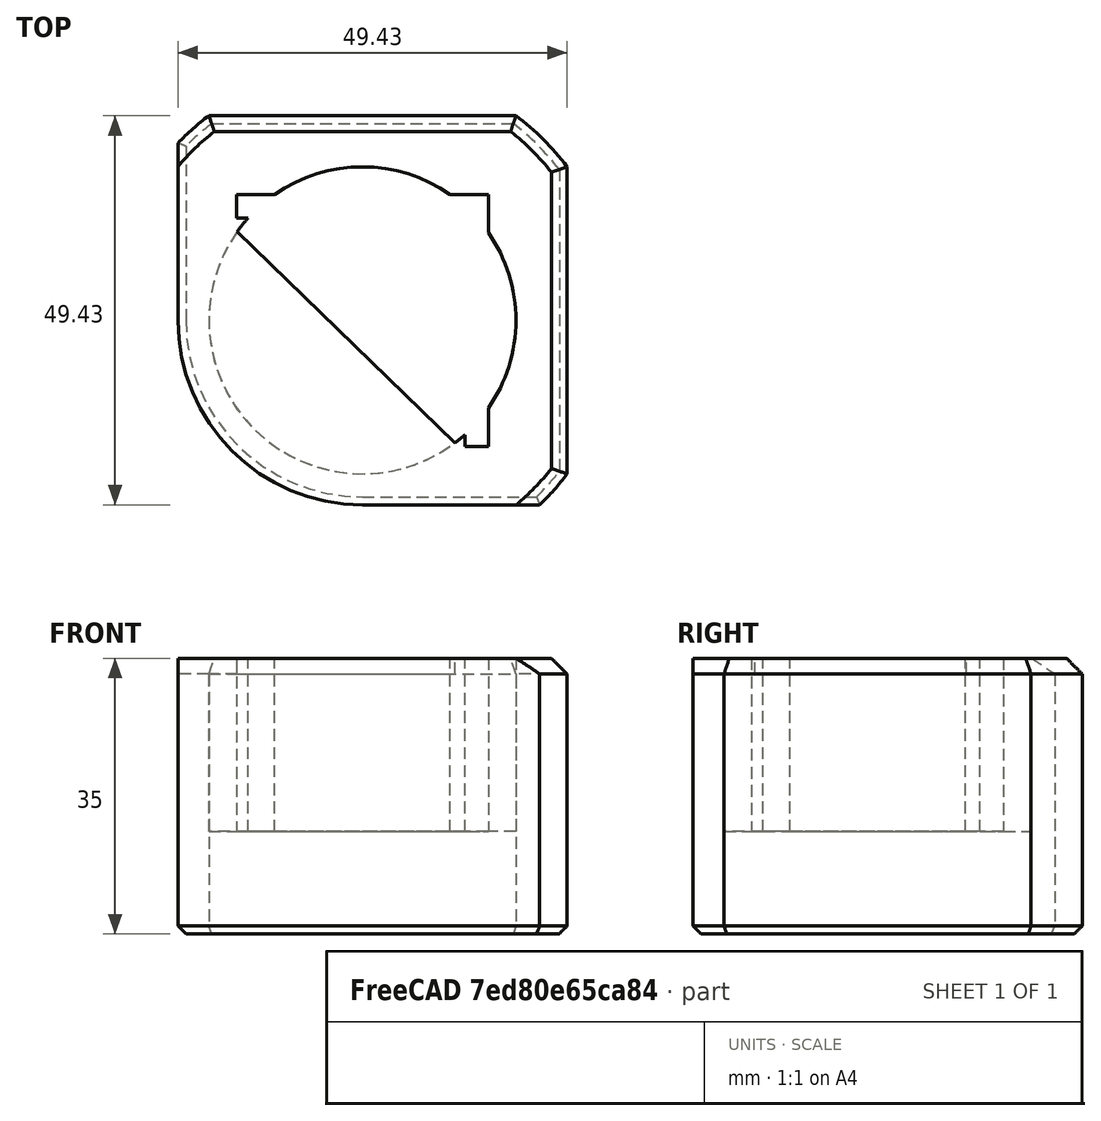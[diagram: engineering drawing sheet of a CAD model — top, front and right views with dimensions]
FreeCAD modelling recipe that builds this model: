
FCSTD DOCUMENT  (FreeCAD 0.19R)
Label: tankfeettallRC1
License: All rights reserved
LicenseURL: http://en.wikipedia.org/wiki/All_rights_reserved
objects: Sketcher::SketchObject×6, PartDesign::Pocket×4, PartDesign::Pad×2, PartDesign::Chamfer×2, PartDesign::Body×1, Mesh::Feature×1
note: 23 computed .brp shape members not serialized (recipe doc carries the construction recipe); baked Part::Feature solids carry a one-line shape summary decoded from their .brp

FEATURE [Sketcher::SketchObject] Sketch
  FullyConstrained = true
  MapMode = 5
  Support = -> [XY_Plane]
  sketch-geometry (1):
    g0: Circle CenterX=0 CenterY=0 CenterZ=0 NormalX=0 NormalY=0 NormalZ=1 AngleXU=0 Radius=32.5
  constraints (2):
    c: Coincident(g0,g-1)
    c: Diameter(g0) = 65
FEATURE [PartDesign::Pad] Pad
  Direction = (1,1,1)
  Length = 35
  Length2 = 100
  Profile = -> Sketch
  Type = 0
FEATURE [Sketcher::SketchObject] Sketch001
  FullyConstrained = true
  MapMode = 5
  Placement = pos=(0,0,35) rot=(0,0,1;0rad)
  Support = -> [Pad]
  sketch-geometry (10):
    g0: LineSegment StartX=-16 StartY=16 StartZ=0 EndX=16 EndY=16 EndZ=0
    g1: LineSegment StartX=16 StartY=16 StartZ=0 EndX=16 EndY=-16 EndZ=0
    g2: LineSegment StartX=16 StartY=-16 StartZ=0 EndX=-16 EndY=-16 EndZ=0
    g3: LineSegment StartX=-16 StartY=-16 StartZ=0 EndX=-16 EndY=16 EndZ=0
    g4: LineSegment StartX=-16 StartY=16 StartZ=0 EndX=16 EndY=16 EndZ=0
    g5: LineSegment StartX=16 StartY=16 StartZ=0 EndX=16 EndY=-16 EndZ=0
    g6: LineSegment StartX=16 StartY=-16 StartZ=0 EndX=13 EndY=-16 EndZ=0
    g7: LineSegment StartX=13 StartY=-16 StartZ=0 EndX=13 EndY=13 EndZ=0
    g8: LineSegment StartX=13 StartY=13 StartZ=0 EndX=-16 EndY=13 EndZ=0
    g9: LineSegment StartX=-16 StartY=13 StartZ=0 EndX=-16 EndY=16 EndZ=0
  constraints (27):
    c: Coincident(g0,g1)
    c: Coincident(g1,g2)
    c: Coincident(g2,g3)
    c: Coincident(g3,g0)
    c: Horizontal(g0)
    c: Horizontal(g2)
    c: Vertical(g1)
    c: Vertical(g3)
    c: Symmetric(g1,g0,g-1)
    c: Distance(g0) = 32
    c: Equal(g1,g0)
    c: Coincident(g4,g5)
    c: Coincident(g5,g6)
    c: Coincident(g6,g7)
    c: Vertical(g7)
    c: Coincident(g7,g8)
    c: Horizontal(g8)
    c: Coincident(g8,g9)
    c: Coincident(g9,g4)
    c: Vertical(g9)
    c: Distance(g9) = 3
    c: Equal(g6,g9)
    c: Horizontal(g6)
    c: Symmetric(g4,g4,g-2)
    c: Symmetric(g5,g4,g-1)
    c: Distance(g4) = 32
    c: Equal(g5,g4)
FEATURE [PartDesign::Pocket] Pocket
  BaseFeature = -> Pad
  Length = 22
  Length2 = 100
  Profile = -> Sketch001
  Type = 0
FEATURE [Sketcher::SketchObject] Sketch002
  FullyConstrained = true
  MapMode = 5
  Placement = pos=(0,0,35) rot=(0,0,1;0rad)
  Support = -> [Pocket]
  sketch-geometry (1):
    g0: Circle CenterX=0 CenterY=0 CenterZ=0 NormalX=0 NormalY=0 NormalZ=1 AngleXU=0 Radius=19.5
  constraints (2):
    c: Coincident(g0,g-1)
    c: Diameter(g0) = 39
FEATURE [PartDesign::Pocket] Pocket001
  BaseFeature = -> Pocket
  Length = 22
  Length2 = 100
  Profile = -> Sketch002
  Type = 0
FEATURE [Sketcher::SketchObject] Sketch003
  FullyConstrained = false
  MapMode = 5
  Placement = pos=(0,0,35) rot=(0,0,1;0rad)
  Support = -> [Pocket001]
  sketch-geometry (10):
    g0: LineSegment StartX=26 StartY=26 StartZ=0 EndX=26 EndY=-26 EndZ=0
    g1: LineSegment StartX=26 StartY=-26 StartZ=0 EndX=67.4944 EndY=-26 EndZ=0
    g2: LineSegment StartX=67.4944 StartY=-26 StartZ=0 EndX=72.3472 EndY=49.8195 EndZ=0
    g3: LineSegment StartX=72.3472 StartY=49.8195 StartZ=0 EndX=-56.3282 EndY=49.8195 EndZ=0
    g4: LineSegment StartX=-56.3282 StartY=49.8195 StartZ=0 EndX=-56.3282 EndY=-44.3399 EndZ=0
    g5: LineSegment StartX=-56.3282 StartY=-44.3399 StartZ=0 EndX=22.1064 EndY=-44.3399 EndZ=0
    g6: LineSegment StartX=22.1064 StartY=-44.3399 StartZ=0 EndX=27.22 EndY=-26 EndZ=0
    g7: LineSegment StartX=27.22 StartY=-26 StartZ=0 EndX=-26 EndY=-26 EndZ=0
    g8: LineSegment StartX=-26 StartY=-26 StartZ=0 EndX=-26 EndY=26 EndZ=0
    g9: LineSegment StartX=-26 StartY=26 StartZ=0 EndX=26 EndY=26 EndZ=0
  constraints (22):
    c: Vertical(g0)
    c: Coincident(g0,g1)
    c: Horizontal(g1)
    c: Coincident(g1,g2)
    c: Coincident(g2,g3)
    c: Horizontal(g3)
    c: Coincident(g3,g4)
    c: Vertical(g4)
    c: Coincident(g4,g5)
    c: Horizontal(g5)
    c: Coincident(g5,g6)
    c: Coincident(g6,g7)
    c: Horizontal(g7)
    c: Coincident(g7,g8)
    c: Coincident(g8,g9)
    c: Coincident(g9,g0)
    c: Symmetric(g0,g8,g-2)
    c: Symmetric(g8,g7,g-1)
    c: Distance(g8) = 52
    c: Distance(g9) = 52
    c: Distance(g0) = 52
    c: Distance(g7) = 53.22
FEATURE [PartDesign::Pocket] Pocket002
  BaseFeature = -> Pocket001
  Length = 5
  Length2 = 100
  Profile = -> Sketch003
  Type = 1
FEATURE [Sketcher::SketchObject] Sketch004
  FullyConstrained = false
  MapMode = 5
  Placement = pos=(0,0,35) rot=(0,0,1;0rad)
  Support = -> [Pocket002]
  sketch-geometry (2):
    g0: ArcOfCircle CenterX=0 CenterY=0 CenterZ=0 NormalX=0 NormalY=0 NormalZ=1 AngleXU=0 Radius=22.0943 StartAngle=2.50673 EndAngle=5.37592
    g1: LineSegment StartX=-17.7893 StartY=13.1034 StartZ=0 EndX=13.6079 EndY=-17.4064 EndZ=0
  constraints (4):
    c: Coincident(g0,g-1)
    c: Coincident(g1,g0)
    c: Coincident(g1,g0)
    c: Distance(g0,g1) = 3
FEATURE [PartDesign::Pad] Pad001
  BaseFeature = -> Pocket002
  Direction = (1,1,1)
  Length = 2
  Length2 = 100
  Profile = -> Sketch004
  Reversed = true
  Type = 0
FEATURE [Sketcher::SketchObject] Sketch005
  FullyConstrained = false
  MapMode = 5
  Placement = pos=(0,0,35) rot=(0,0,1;0rad)
  Support = -> [Pad001]
  sketch-geometry (5):
    g0: ArcOfCircle CenterX=0 CenterY=0 CenterZ=0 NormalX=0 NormalY=0 NormalZ=1 AngleXU=0 Radius=23.4313 StartAngle=3.14159 EndAngle=4.71239
    g1: LineSegment StartX=-23.4313 StartY=2.9e-15 StartZ=0 EndX=-23.4313 EndY=32.6981 EndZ=0
    g2: LineSegment StartX=-23.4313 StartY=32.6981 StartZ=0 EndX=-71.4663 EndY=-64.3554 EndZ=0
    g3: LineSegment StartX=-4.3e-15 StartY=-23.4313 StartZ=0 EndX=33.6024 EndY=-23.4313 EndZ=0
    g4: LineSegment StartX=33.6024 StartY=-23.4313 StartZ=0 EndX=-71.4663 EndY=-64.3554 EndZ=0
  constraints (8):
    c: Coincident(g0,g-1)
    c: PointOnObject(g0,g-1)
    c: PointOnObject(g0,g-2)
    c: Tangent(g0,g1) = 1.5708
    c: Coincident(g1,g2)
    c: Tangent(g0,g3) = -1.5708
    c: Coincident(g3,g4)
    c: Coincident(g4,g2)
FEATURE [PartDesign::Pocket] Pocket003
  BaseFeature = -> Pad001
  Length = 5
  Length2 = 100
  Profile = -> Sketch005
  Type = 1
FEATURE [PartDesign::Chamfer] Chamfer
  Angle = 45
  Base = -> Pocket003 [Edge12,Edge19,Edge3,Edge14,Edge15]
  BaseFeature = -> Pocket003
  ChamferType = 0
  FlipDirection = false
  Size = 2
  Size2 = 1
  SupportTransform = false
FEATURE [PartDesign::Chamfer] Chamfer001
  Angle = 45
  Base = -> Chamfer [Face4]
  BaseFeature = -> Chamfer
  ChamferType = 0
  FlipDirection = false
  Size = 1
  Size2 = 1
  SupportTransform = false
FEATURE [PartDesign::Body] Body
  Group = -> [Sketch,Pad,Sketch001,Pocket,Sketch002,Pocket001,Sketch003,Pocket002,Sketch004,Pad001,Sketch005,Pocket003,Chamfer,Chamfer001]
  Origin = -> Origin
  Tip = -> Chamfer001
FEATURE [Mesh::Feature] Mesh  label="Chamfer001 (Meshed)"
